# Revit family: CENTUM Spannschloss DIN1480 geschmiedet M12
name_source: partatom
category: HLS-Bauteile
revit_build: Autodesk Revit 2017 (Build: 20190507_1515(x64)
units: mm (PartAtom-declared; Revit-internal decimal feet)

## family parameters
Arbeitsebenenbasiert = Ja
Beim Laden mit Abzugskörper schneiden = Nein
Bemaßung runder Anschluss = Durchmesser verwenden
Gemeinsam genutzt = Ja
Immer vertikal = Nein
Raumberechnungspunkt = Nein
Teiletyp = Normal

## types (1)
- CENTUM Spannschloss DIN 1480 geschmiedet M12
    Artikelnummer = 1660007452
    Außendurchmesser = 34 mm
    EAN = 4250928449573
    Fabrikat = MEFA
    Firma = MEFA Befestigungs- und Montagesysteme GmbH
    Gewicht = 0.25 kg
    Gewicht pro Bauteil = 0.25 kg
    Gewinde = M12
    Kurztext1 = Spannschloss offen DIN 1480
    Kurztext2 = M12 fsv
    Länge = 125 mm  [stored 0.410105 ft]
    Material = Stahl
    Mengeneinheit = St
    Nachstellbarkeit = 80 mm
    Oberflaeche = feuerstückverzinkt
    Vorgabe-Ansicht = 1219 mm
    max. zul. Last = 9.30 kN
    vpe = 1 St

note: [stored X ft] marks values corroborated as IEEE doubles in the binary element streams (Revit-internal decimal feet)
